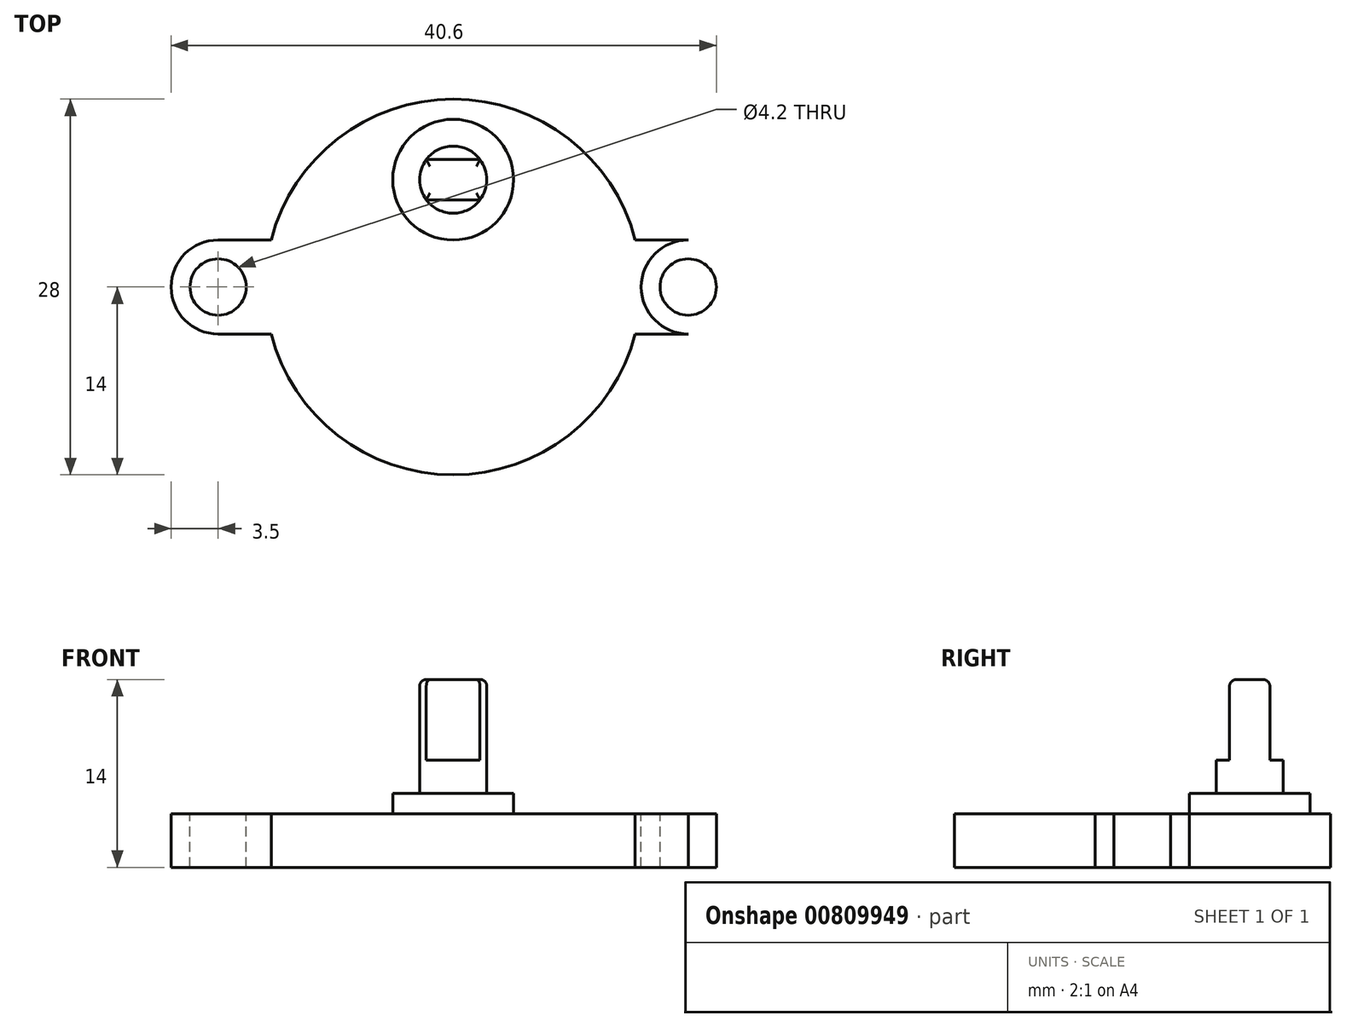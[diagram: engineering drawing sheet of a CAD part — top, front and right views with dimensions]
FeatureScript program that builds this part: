
annotation { "Feature Type Name" : "Feature", "Feature Type Description" : "" }
export const myFeature = defineFeature(function(context is Context, id is Id, definition is map)
    precondition{}
    {
        {
            var Q0;
            Q0=qCreatedBy(makeId("Top.planeOp"),FACE);
            var sketch = newSketch(context, id + "F0", { "sketchPlane" : qUnion([Q0])});
            skCircle(sketch, "E0", {"center": v(0, 0) * mm, "radius": 14 * mm});
            skCircle(sketch, "E1", {"center": v(-17.5, 0) * mm, "radius": 2.1 * mm});
            skCircle(sketch, "E2.MirrorC", {"center": v(17.5, 0) * mm, "radius": 2.1 * mm});
            skCircle(sketch, "E3", {"center": v(0, 8) * mm, "radius": 4.5 * mm});
            skCircle(sketch, "E4", {"center": v(0, 8) * mm, "radius": 2.5 * mm});
            skLineSegment(sketch, "E5", {"start": v(-2, 9.5) * mm, "end": v(2, 9.5) * mm});
            skLineSegment(sketch, "E6", {"start": v(0, 8) * mm, "end": v(1.5, 8) * mm, "construction": true});
            skLineSegment(sketch, "E7.MirrorCS", {"start": v(-2, 6.5) * mm, "end": v(2, 6.5) * mm});
            skCircle(sketch, "E8", {"center": v(-17.5, 0) * mm, "radius": 3.5 * mm});
            skLineSegment(sketch, "E9", {"start": v(-17.5, 3.5) * mm, "end": v(-13.56, 3.5) * mm});
            skLineSegment(sketch, "E10", {"start": v(-17.5, -3.5) * mm, "end": v(-13.56, -3.5) * mm});
            skLineSegment(sketch, "E11.MirrorCS", {"start": v(17.5, 3.5) * mm, "end": v(13.56, 3.5) * mm});
            skLineSegment(sketch, "E12.MirrorCS", {"start": v(17.5, -3.5) * mm, "end": v(13.56, -3.5) * mm});
            skCircle(sketch, "E13.MirrorC", {"center": v(17.5, 0) * mm, "radius": 3.5 * mm});
            skSolve(sketch);
        }
        {
            var Q0;
            {var subQ0=sQuery(id+"F0.wireOp",EDGE,"E5");Q0=makeQuery(id+"F0.imprint","IMPRINT",FACE,{"disambiguationData":[TD([[makeQuery(id+"F0.imprint","IMPRINT",EDGE,{"derivedFrom":subQ0}),-1.0]])]});}
            extrude(context, id + "F1", {"entities" : qUnion([Q0]), "depth" : 10 * mm, "offsetDistance" : 25 * mm});
        }
        {
            var Q0;
            {var subQ0=sQuery(id+"F0.wireOp",EDGE,"E7.MirrorCS");Q0=makeQuery(id+"F0.imprint","IMPRINT",FACE,{"disambiguationData":[TD([[makeQuery(id+"F0.imprint","IMPRINT",EDGE,{"derivedFrom":subQ0}),-1.0]])]});}
            var Q1;
            {var subQ0=sQuery(id+"F0.wireOp",EDGE,"E5");Q1=makeQuery(id+"F0.imprint","IMPRINT",FACE,{"disambiguationData":[TD([[makeQuery(id+"F0.imprint","IMPRINT",EDGE,{"derivedFrom":subQ0}),1.0]])]});}
            extrude(context, id + "F2", {"entities" : qUnion([Q0, Q1]), "operationType" : NewBodyOperationType.ADD, "depth" : 4 * mm, "offsetDistance" : 25 * mm});
        }
        {
            var Q0;
            Q0=makeQuery(id+"F0.imprint","IMPRINT",FACE,{"disambiguationData":[TD([[makeQuery(id+"F0.imprint","IMPRINT",EDGE,{"derivedFrom":sQuery(id+"F0.wireOp",EDGE,"E3")}),1.0]])]});
            extrude(context, id + "F3", {"entities" : qUnion([Q0]), "operationType" : NewBodyOperationType.ADD, "depth" : 1.5 * mm, "offsetDistance" : 25 * mm});
        }
        {
            var Q0;
            Q0=makeQuery(id+"F1.opExtrude","CAP_EDGE",EDGE,{"disambiguationData":[OSD([sQuery(id+"F0.wireOp",EDGE,"E5")])],"isStart":false});
            var Q1;
            Q1=makeQuery(id+"F1.opExtrude","CAP_EDGE",EDGE,{"disambiguationData":[OSD([sQuery(id+"F0.wireOp",EDGE,"E7.MirrorCS")])],"isStart":false});
            var Q2;
            {var subQ0=sQuery(id+"F0.wireOp",EDGE,"E4");Q2=makeQuery(id+"F1.opExtrude","CAP_EDGE",EDGE,{"disambiguationData":[OSD([subQ0]),TDD([makeQuery(id+"F0.imprint","IMPRINT",EDGE,{"disambiguationData":[TD([[makeQuery(id+"F0.imprint","INTERSECT",VERTEX,{"disambiguationData":[OD(0.0)],"derivedFrom":[subQ0,sQuery(id+"F0.wireOp",EDGE,"E5")]}),-1.0]])],"derivedFrom":subQ0})])],"isStart":false});}
            var Q3;
            {var subQ0=sQuery(id+"F0.wireOp",EDGE,"E4");Q3=makeQuery(id+"F1.opExtrude","CAP_EDGE",EDGE,{"disambiguationData":[OSD([subQ0]),TDD([makeQuery(id+"F0.imprint","IMPRINT",EDGE,{"disambiguationData":[TD([[makeQuery(id+"F0.imprint","INTERSECT",VERTEX,{"disambiguationData":[OD(1.0)],"derivedFrom":[subQ0,sQuery(id+"F0.wireOp",EDGE,"E5")]}),1.0]])],"derivedFrom":subQ0})])],"isStart":false});}
            fillet(context, id + "F4", {"entities" : qUnion([Q0, Q1, Q2, Q3]), "radius" : .5 * mm, "tangentPropagation" : true, "allowEdgeOverflow" : false});
        }
        {
            var Q0;
            Q0=makeQuery(id+"F0.imprint","IMPRINT",FACE,{"disambiguationData":[TD([[makeQuery(id+"F0.imprint","IMPRINT",EDGE,{"derivedFrom":sQuery(id+"F0.wireOp",EDGE,"E3")}),-1.0]])]});
            var Q1;
            Q1=makeQuery(id+"F0.imprint","IMPRINT",FACE,{"disambiguationData":[TD([[makeQuery(id+"F0.imprint","IMPRINT",EDGE,{"derivedFrom":sQuery(id+"F0.wireOp",EDGE,"E1")}),-1.0]])]});
            var Q2;
            {var subQ0=sQuery(id+"F0.wireOp",EDGE,"E9");Q2=makeQuery(id+"F0.imprint","IMPRINT",FACE,{"disambiguationData":[TD([[makeQuery(id+"F0.imprint","IMPRINT",EDGE,{"derivedFrom":subQ0}),-1.0]])]});}
            var Q3;
            {var subQ0=sQuery(id+"F0.wireOp",EDGE,"E10");Q3=makeQuery(id+"F0.imprint","IMPRINT",FACE,{"disambiguationData":[TD([[makeQuery(id+"F0.imprint","IMPRINT",EDGE,{"derivedFrom":subQ0}),1.0]])]});}
            var Q4;
            Q4=makeQuery(id+"F0.imprint","IMPRINT",FACE,{"disambiguationData":[TD([[makeQuery(id+"F0.imprint","IMPRINT",EDGE,{"derivedFrom":sQuery(id+"F0.wireOp",EDGE,"E2.MirrorC")}),1.0]])]});
            var Q5;
            {var subQ0=sQuery(id+"F0.wireOp",EDGE,"E11.MirrorCS");Q5=makeQuery(id+"F0.imprint","IMPRINT",FACE,{"disambiguationData":[TD([[makeQuery(id+"F0.imprint","IMPRINT",EDGE,{"derivedFrom":subQ0}),1.0]])]});}
            var Q6;
            {var subQ0=sQuery(id+"F0.wireOp",EDGE,"E12.MirrorCS");Q6=makeQuery(id+"F0.imprint","IMPRINT",FACE,{"disambiguationData":[TD([[makeQuery(id+"F0.imprint","IMPRINT",EDGE,{"derivedFrom":subQ0}),-1.0]])]});}
            var Q7;
            Q7=makeQuery(id+"F0.imprint","IMPRINT",FACE,{"disambiguationData":[TD([[makeQuery(id+"F0.imprint","IMPRINT",EDGE,{"derivedFrom":sQuery(id+"F0.wireOp",EDGE,"E3")}),1.0]])]});
            var Q8;
            {var subQ0=sQuery(id+"F0.wireOp",EDGE,"E5");Q8=makeQuery(id+"F0.imprint","IMPRINT",FACE,{"disambiguationData":[TD([[makeQuery(id+"F0.imprint","IMPRINT",EDGE,{"derivedFrom":subQ0}),-1.0]])]});}
            var Q9;
            {var subQ0=sQuery(id+"F0.wireOp",EDGE,"E7.MirrorCS");Q9=makeQuery(id+"F0.imprint","IMPRINT",FACE,{"disambiguationData":[TD([[makeQuery(id+"F0.imprint","IMPRINT",EDGE,{"derivedFrom":subQ0}),-1.0]])]});}
            var Q10;
            {var subQ0=sQuery(id+"F0.wireOp",EDGE,"E5");Q10=makeQuery(id+"F0.imprint","IMPRINT",FACE,{"disambiguationData":[TD([[makeQuery(id+"F0.imprint","IMPRINT",EDGE,{"derivedFrom":subQ0}),1.0]])]});}
            extrude(context, id + "F5", {"entities" : qUnion([Q0, Q1, Q2, Q3, Q4, Q5, Q6, Q7, Q8, Q9, Q10]), "operationType" : NewBodyOperationType.ADD, "oppositeDirection" : true, "depth" : 4 * mm, "offsetDistance" : 25 * mm});
        }
    });
